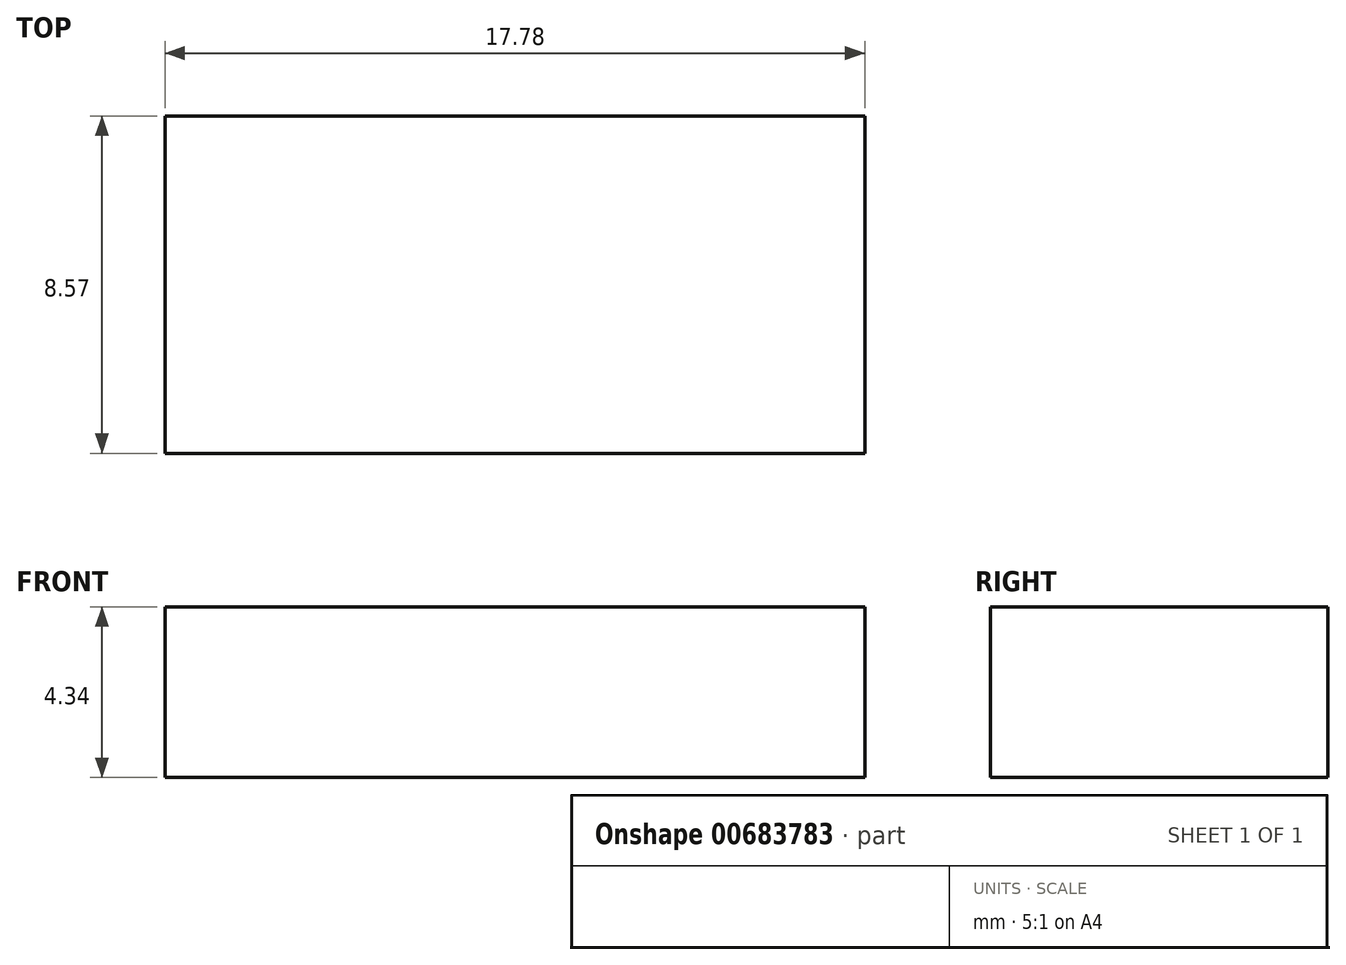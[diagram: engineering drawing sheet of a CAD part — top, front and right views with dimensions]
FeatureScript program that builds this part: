
annotation { "Feature Type Name" : "Feature", "Feature Type Description" : "" }
export const myFeature = defineFeature(function(context is Context, id is Id, definition is map)
    precondition{}
    {
        {
            var Q0;
            Q0=qCreatedBy(makeId("Right.planeOp"),FACE);
            var sketch = newSketch(context, id + "F0", { "sketchPlane" : qUnion([Q0])});
            skLineSegment(sketch, "E0.bottom", {"start": v(0, 14.02) * mm, "end": v(-8.57, 14.02) * mm});
            skLineSegment(sketch, "E0.top", {"start": v(0, 18.36) * mm, "end": v(-8.57, 18.36) * mm});
            skLineSegment(sketch, "E0.left", {"start": v(0, 14.02) * mm, "end": v(0, 18.36) * mm});
            skLineSegment(sketch, "E0.right", {"start": v(-8.57, 14.02) * mm, "end": v(-8.57, 18.36) * mm});
            skSolve(sketch);
        }
        {
            var Q0;
            Q0=makeQuery(id+"F0.imprint","IMPRINT",FACE,{"disambiguationData":[TD([[makeQuery(id+"F0.imprint","IMPRINT",EDGE,{"derivedFrom":sQuery(id+"F0.wireOp",EDGE,"E0.bottom")}),-1.0]])]});
            extrude(context, id + "F1", {"entities" : qUnion([Q0]), "oppositeDirection" : true, "depth" : 17.78 * mm, "offsetDistance" : 25.4 * mm});
        }
    });
